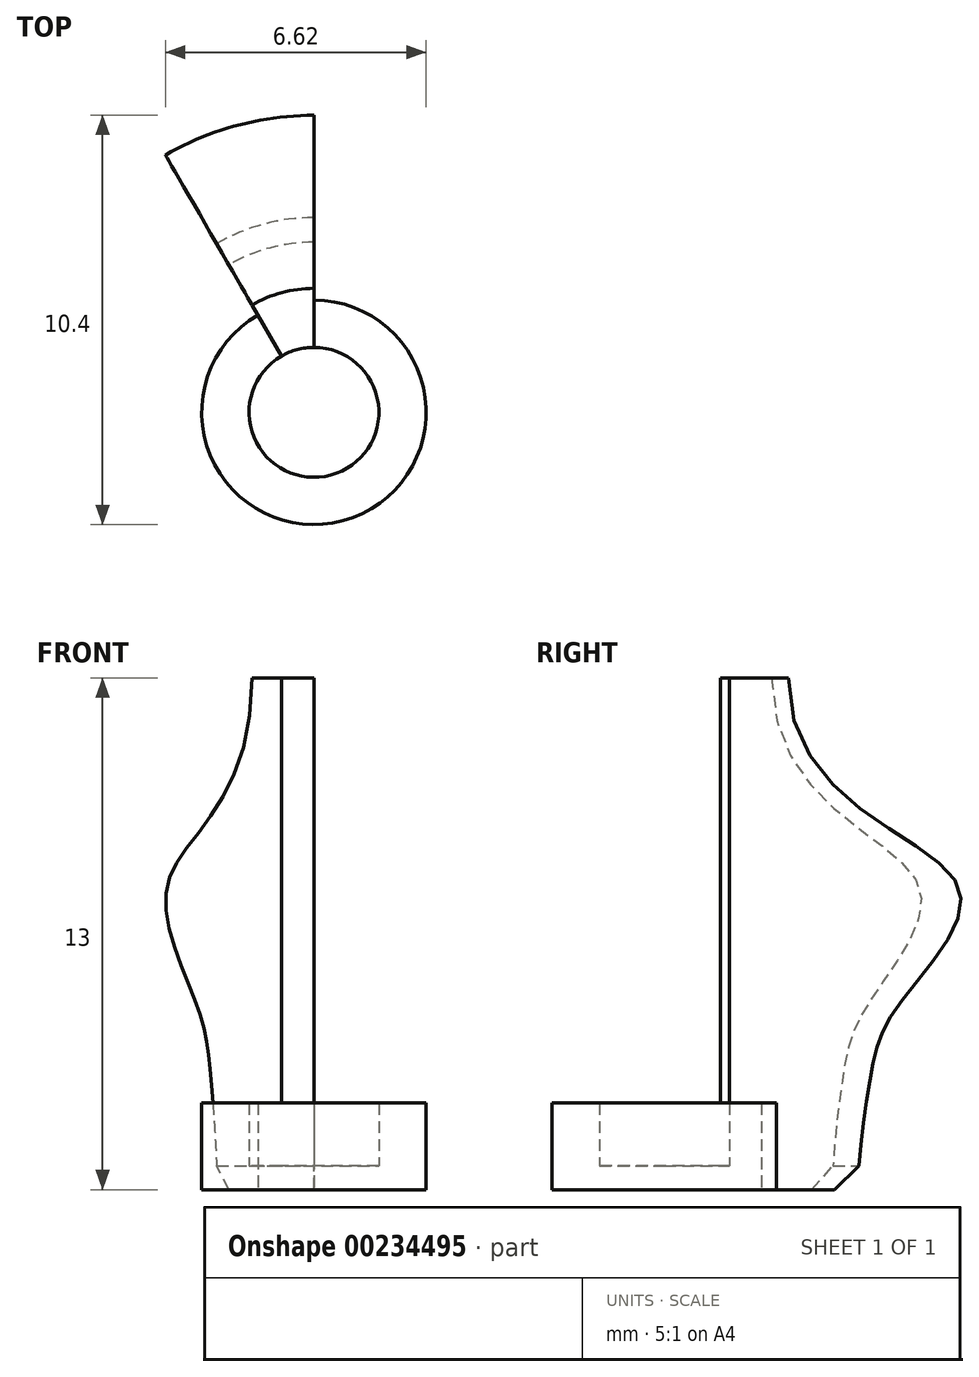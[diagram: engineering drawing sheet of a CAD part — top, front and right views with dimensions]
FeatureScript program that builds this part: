
annotation { "Feature Type Name" : "Feature", "Feature Type Description" : "" }
export const myFeature = defineFeature(function(context is Context, id is Id, definition is map)
    precondition{}
    {
        {
            var Q0;
            Q0=qCreatedBy(makeId("Top.planeOp"),FACE);
            var sketch = newSketch(context, id + "F0", { "sketchPlane" : qUnion([Q0]), "disableImprinting" : false});
            skCircle(sketch, "E0", {"center": v(0, 0) * mm, "radius": 1.65 * mm});
            skCircle(sketch, "E1.0", {"center": v(0, 0) * mm, "radius": 2.85 * mm});
            skSolve(sketch);
        }
        {
            var Q0;
            Q0 = qSketchRegion(id + "F0", true);
            extrude(context, id + "F1", {"entities" : qUnion([Q0]), "flatOperationType" : FlatOperationType.REMOVE, "thickness1" : 5 * mm, "thickness2" : 0 * mm, "offsetDistance" : 25 * mm, "startOffsetBound" : StartOffsetType.BLIND, "startOffsetDistance" : 25 * mm, "depth" : 1.6 * mm, "domain" : OperationDomain.MODEL});
        }
        {
            var Q0;
            Q0=qCreatedBy(makeId("Top.planeOp"),FACE);
            var sketch = newSketch(context, id + "F2", { "sketchPlane" : qUnion([Q0]), "disableImprinting" : false});
            skCircle(sketch, "E2.0", {"center": v(0, 0) * mm, "radius": 2.85 * mm});
            skSolve(sketch);
        }
        {
            var Q0;
            Q0 = qSketchRegion(id + "F2", true);
            extrude(context, id + "F3", {"entities" : qUnion([Q0]), "operationType" : NewBodyOperationType.ADD, "flatOperationType" : FlatOperationType.REMOVE, "thickness1" : 5 * mm, "thickness2" : 0 * mm, "oppositeDirection" : true, "offsetDistance" : 25 * mm, "startOffsetBound" : StartOffsetType.BLIND, "startOffsetDistance" : 25 * mm, "depth" : 0.6 * mm, "domain" : OperationDomain.MODEL});
        }
        {
            var Q0;
            Q0=qCreatedBy(makeId("Right.planeOp"),FACE);
            var sketch = newSketch(context, id + "F4", { "sketchPlane" : qUnion([Q0]), "disableImprinting" : false});
            skLineSegment(sketch, "E3", {"start": v(1.65, -0.6) * mm, "end": v(4.92, -0.6) * mm});
            skLineSegment(sketch, "E4", {"start": v(1.65, -0.6) * mm, "end": v(1.65, 12.4) * mm});
            skLineSegment(sketch, "E5", {"start": v(1.65, 12.4) * mm, "end": v(3.15, 12.4) * mm});
            skFitSpline(sketch, "E6", {"points": [v(3.15, 12.4) * mm, v(7.48, 7.08) * mm, v(5.95, 4.08) * mm, v(5.24, 2.26) * mm, v(4.92, -0.6) * mm], "startDerivative": vector(0, -28.83) * mm, "endDerivative": vector(0, -10.62) * mm});
            skLineSegment(sketch, "E7", {"start": v(0, 0) * mm, "end": v(0, 12.4) * mm, "construction": true});
            skPoint(sketch, "E7.endSnap0", {"position": v(2.4, 12.4) * mm});
            skSolve(sketch);
        }
        {
            var Q0;
            Q0 = qSketchRegion(id + "F4", true);
            var Q1;
            Q1=sQuery(id+"F4.wireOp",EDGE,"E7");
            revolve(context, id + "F5", {"operationType" : NewBodyOperationType.ADD, "surfaceOperationType" : NewSurfaceOperationType.NEW, "entities" : qUnion([Q0]), "axis" : qUnion([Q1]), "revolveType" : RevolveType.ONE_DIRECTION, "angle" : 30 * degree});
        }
        {
            var Q0;
            Q0=makeQuery(id+"F5.opRevolve","SWEPT_EDGE",EDGE,{"disambiguationData":[OSD([sQuery(id+"F4.wireOp",EDGE,"E3"),sQuery(id+"F4.wireOp",EDGE,"E6")])]});
            chamfer(context, id + "F6", {"entities" : qUnion([Q0]), "width" : 0.6 * mm, "tangentPropagation" : true});
        }
    });
